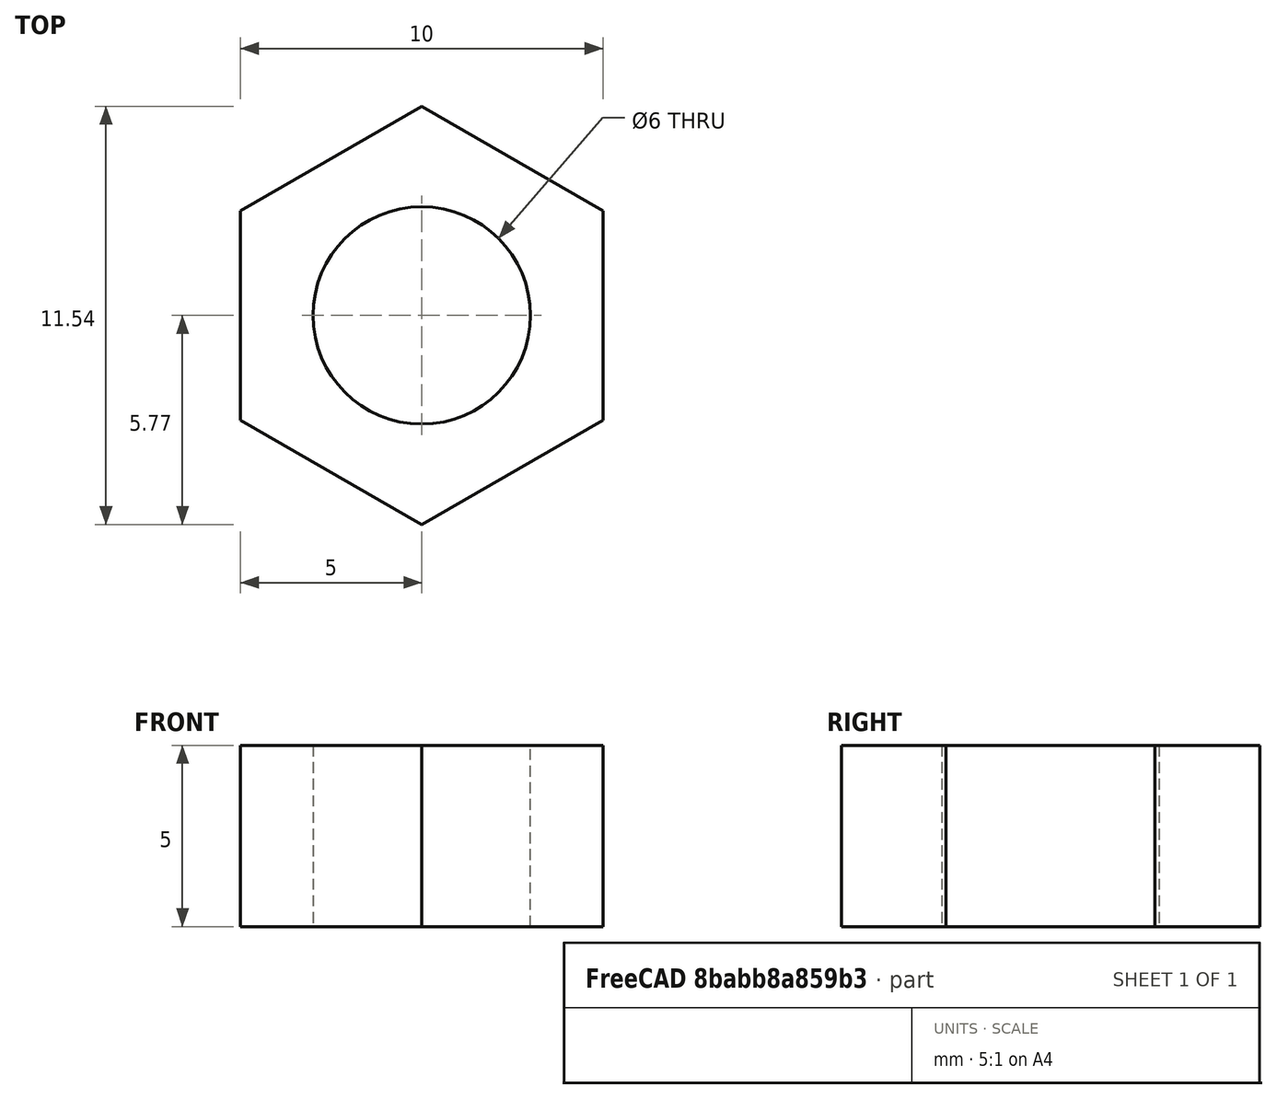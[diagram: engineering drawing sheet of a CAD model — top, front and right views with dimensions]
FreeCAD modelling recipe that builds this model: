
FCSTD DOCUMENT  (FreeCAD 0.18.4R)
Label: m6_full_nut
License: All rights reserved
LicenseURL: http://en.wikipedia.org/wiki/All_rights_reserved
objects: Sketcher::SketchObject×1, PartDesign::Pad×1, PartDesign::Body×1
note: 4 computed .brp shape members not serialized (recipe doc carries the construction recipe); baked Part::Feature solids carry a one-line shape summary decoded from their .brp

FEATURE [Sketcher::SketchObject] Sketch
  MapMode = 5
  Support = -> [XY_Plane]
  sketch-geometry (8):
    g0: LineSegment StartX=0 StartY=5.7735 StartZ=0 EndX=-5 EndY=2.88675 EndZ=0
    g1: LineSegment StartX=-5 StartY=2.88675 StartZ=0 EndX=-5 EndY=-2.88675 EndZ=0
    g2: LineSegment StartX=-5 StartY=-2.88675 StartZ=0 EndX=-1.501e-13 EndY=-5.7735 EndZ=0
    g3: LineSegment StartX=-1.501e-13 StartY=-5.7735 StartZ=0 EndX=5 EndY=-2.88675 EndZ=0
    g4: LineSegment StartX=5 StartY=-2.88675 StartZ=0 EndX=5 EndY=2.88675 EndZ=0
    g5: LineSegment StartX=5 StartY=2.88675 StartZ=0 EndX=0 EndY=5.7735 EndZ=0
    g6: Circle [constr] CenterX=0 CenterY=0 CenterZ=0 NormalX=0 NormalY=0 NormalZ=1 AngleXU=0 Radius=5.7735
    g7: Circle CenterX=0 CenterY=0 CenterZ=0 NormalX=0 NormalY=0 NormalZ=1 AngleXU=0 Radius=3
  constraints (18):
    c: Coincident(g0,g1)
    c: Coincident(g1,g2)
    c: Coincident(g2,g3)
    c: Coincident(g3,g4)
    c: Coincident(g4,g5)
    c: Coincident(g5,g0)
    c: Equal(g0, g1-g5) x5
    c: PointOnObject(g0,g6)
    c: PointOnObject(g1,g6)
    c: PointOnObject(g2,g6)
    c: PointOnObject(g3,g6)
    c: PointOnObject(g4,g6)
    c: PointOnObject(g5,g6)
    c: Coincident(g6,g-1)
    c: PointOnObject(g0,g-2)
    c: Distance(g0,g4) = 10
    c: Coincident(g7,g-1)
    c: Diameter(g7) = 6
FEATURE [PartDesign::Pad] Pad
  Length = 5
  Length2 = 100
  Profile = -> Sketch
  Type = 0
FEATURE [PartDesign::Body] Body  label="M6_Full_Nut"
  Group = -> [Sketch,Pad]
  Origin = -> Origin
  Tip = -> Pad
